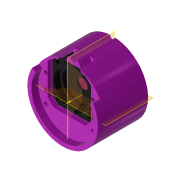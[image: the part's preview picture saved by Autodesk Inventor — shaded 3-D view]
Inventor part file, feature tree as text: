
AUTODESK INVENTOR PART (.ipt)
format: ipt  version: 2022 (Build 260153000, 153)  size: 388,608 bytes
history: native  units: mm
features: reference x20, sketch x7, other x7, extrude x6, plane x3, projected_geometry x3, hole x1
ambient origin geometry x8: Origin, YZ Plane, XZ Plane, XY Plane, X Axis, Y Axis, Z Axis, Center Point
bodies: Volumenkörper1 (feature_tree)
feature tree (47):
  extrude  "Extrusion1"  Depth=2.8mm
  sketch  "Skizze3"  dims[d2=8.0mm d3=0.0mm d4=0.5mm]
  plane  "Arbeitsebene1"
  extrude  "Extrusion2"  Depth=0.5mm
  extrude  "Extrusion3"  Depth=0.5mm
  hole  "Bohrung1"  [1 undecoded]
  extrude  "Extrusion5"  Depth=23.0mm
  other  "Arbeitspunkt1"
  plane  "Arbeitsebene2"
  plane  "Arbeitsebene3"
  extrude  "Extrusion6"  Depth=5.0mm
  extrude  "Extrusion7"  Depth=5.0mm TaperAngle=0.0deg
  sketch  "Skizze1"  dims[d0=2.8mm d1=2.8mm]
  reference  "Referenz1"
  reference  "Referenz2"
  reference  "Referenz3"
  reference  "Referenz4"
  reference  "Referenz5"
  reference  "Referenz7"
  reference  "Referenz8"
  reference  "Referenz9"
  reference  "Referenz10"
  reference  "Referenz11"
  reference  "Referenz12"
  reference  "Referenz13"
  reference  "Referenz14"
  reference  "Referenz15"
  reference  "Referenz16"
  reference  "Referenz17"
  reference  "Referenz18"
  reference  "Referenz19"
  sketch  "Skizze4"  dims[d5=0.5mm d6=0.5mm]
  projected_geometry  "Projizierte Kontur3"
  sketch  "Skizze5"  dims[d7=0.5mm d8=21.0mm d9=0.0mm]
  reference  "Referenz20"
  sketch  "Skizze7"  dims[d10=10.0mm d11=0.0mm]
  reference  "Referenz21"
  projected_geometry  "Projizierte Kontur5"
  other  "Arbeitsachse1"
  sketch  "Skizze8"  dims[d12=2.8mm d13=6.0mm d14=6.5mm d15=23.0mm d16=90.0deg d17=15.0mm d18=20.594885mm d22=0.5mm]
  projected_geometry  "Projizierte Kontur6"
  sketch  "Skizze9"  dims[d23=3.0mm d24=0.0mm d25=46.0mm d26=5.0mm d27=0.0mm d28=4.0mm d29=0.0mm d30=0.0mm]
  other  "MeshFeature1"
  other  "Planktoscope_Mini_Peristalticpump.iam"
  other  "00_Stepper_Motor_28BYJ-48:1"
  other  "Matchboxscope_bottom_v0:1"
  other  "Pump_Lid:1"
note: 1 required parameter value undecoded (feature->parameter linkage not recoverable at this tier; creation-order binding heuristic only, values carry confidence <= 0.55)
